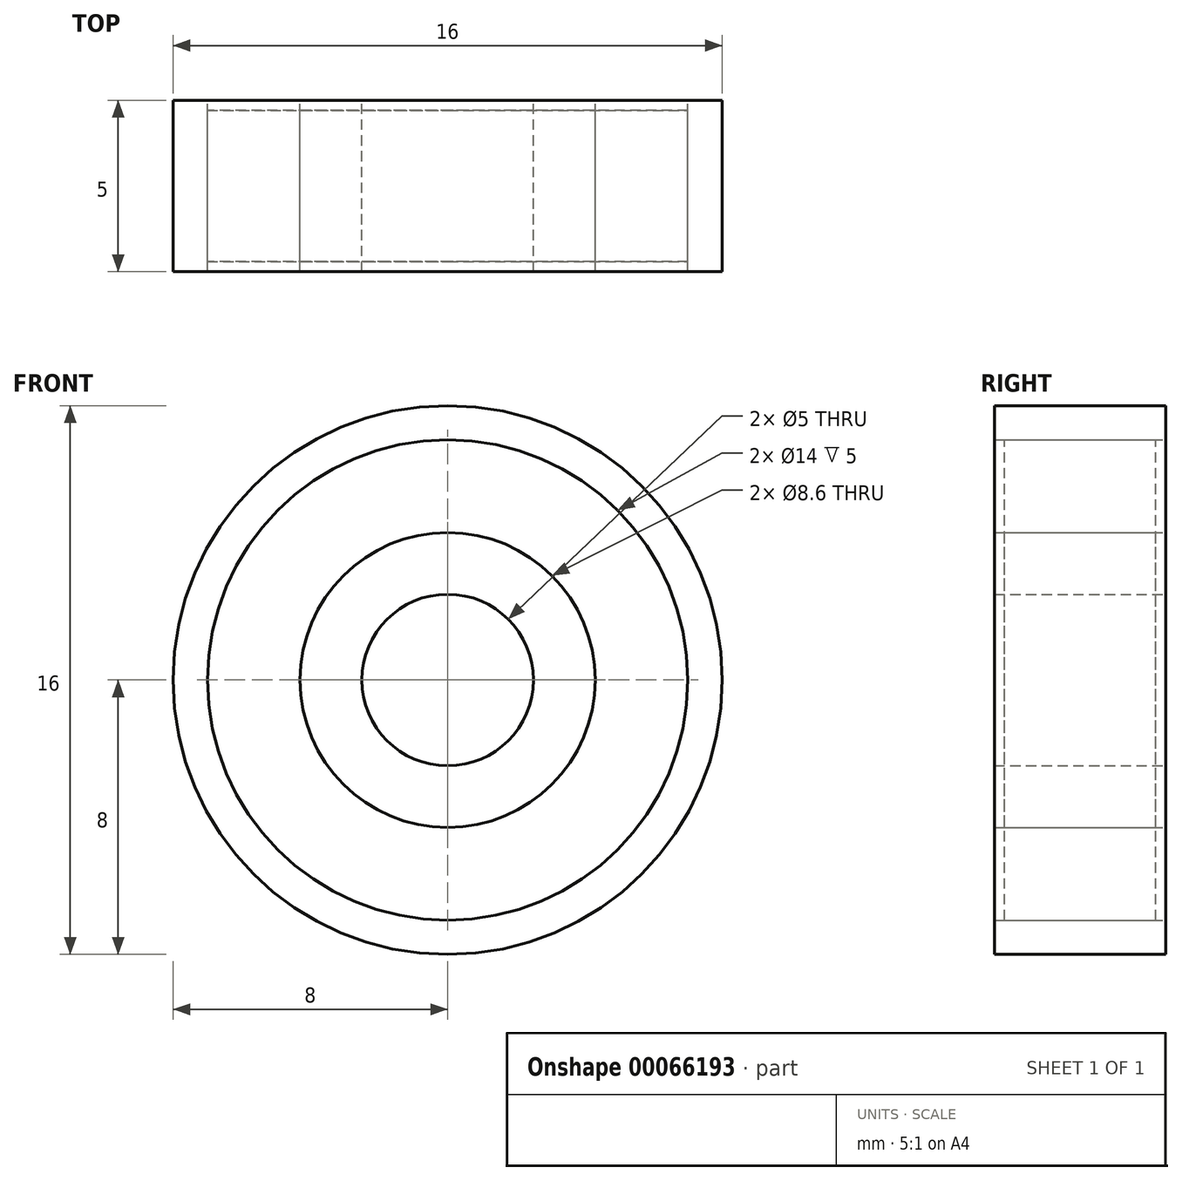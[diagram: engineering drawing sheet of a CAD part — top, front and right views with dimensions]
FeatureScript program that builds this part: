
annotation { "Feature Type Name" : "Feature", "Feature Type Description" : "" }
export const myFeature = defineFeature(function(context is Context, id is Id, definition is map)
    precondition{}
    {
        {
            var Q0;
            Q0=qCreatedBy(makeId("Front.planeOp"),FACE);
            var sketch = newSketch(context, id + "F0", { "sketchPlane" : qUnion([Q0])});
            skCircle(sketch, "E0", {"center": v(0, 0) * mm, "radius": 2.5 * mm});
            skCircle(sketch, "E1", {"center": v(0, 0) * mm, "radius": 4.3 * mm});
            skCircle(sketch, "E2", {"center": v(0, 0) * mm, "radius": 7 * mm});
            skCircle(sketch, "E3", {"center": v(0, 0) * mm, "radius": 8 * mm});
            skSolve(sketch);
        }
        {
            var Q0;
            Q0=makeQuery(id+"F0.imprint","IMPRINT",FACE,{"disambiguationData":[TD([[makeQuery(id+"F0.imprint","IMPRINT",EDGE,{"derivedFrom":sQuery(id+"F0.wireOp",EDGE,"E0")}),-1.0]])]});
            extrude(context, id + "F1", {"entities" : qUnion([Q0]), "depth" : 5 * mm, "symmetric" : true});
        }
        {
            var Q0;
            Q0=makeQuery(id+"F0.imprint","IMPRINT",FACE,{"disambiguationData":[TD([[makeQuery(id+"F0.imprint","IMPRINT",EDGE,{"derivedFrom":sQuery(id+"F0.wireOp",EDGE,"E2")}),-1.0]])]});
            extrude(context, id + "F2", {"entities" : qUnion([Q0]), "depth" : 5 * mm, "symmetric" : true});
        }
        {
            var Q0;
            Q0=makeQuery(id+"F0.imprint","IMPRINT",FACE,{"disambiguationData":[TD([[makeQuery(id+"F0.imprint","IMPRINT",EDGE,{"derivedFrom":sQuery(id+"F0.wireOp",EDGE,"E1")}),-1.0]])]});
            extrude(context, id + "F3", {"entities" : qUnion([Q0]), "depth" : 4.4 * mm, "symmetric" : true});
        }
    });
